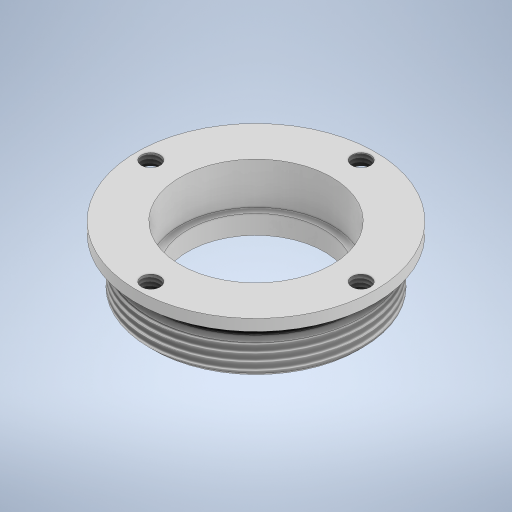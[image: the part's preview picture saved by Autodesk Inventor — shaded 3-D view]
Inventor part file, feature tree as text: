
AUTODESK INVENTOR PART (.ipt)
format: ipt  version: 2023 (Build 270158000, 158)  size: 316,416 bytes
history: native  units: mm
features: sketch x2, revolve x1, chamfer x1, thread x1, hole x1, pattern_circular x1
ambient origin geometry x8: Origin, YZ Plane, XZ Plane, XY Plane, X Axis, Y Axis, Z Axis, Center Point
bodies: Solid1 (feature_tree)
feature tree (7):
  revolve  "Revolution1"  [1 undecoded]
  chamfer  "Chamfer1"  Distance=4.5mm
  thread  "Thread1"  [1 undecoded]
  hole  "Hole2"  [1 undecoded]
  pattern_circular  "Circular Pattern2"  Angle=45.0deg  [1 undecoded]
  sketch  "Sketch1"  dims[d0=18.0mm d2=2.0mm]
  sketch  "Sketch3"  dims[d3=2.0mm d4=4.5mm d5=20.0mm d6=360.0deg d8=0.5mm d9=2.0mm d10=45.0deg d11=3.5mm d12=0.0mm d13=28.0mm d14=1.5mm d15=31.5mm d28=2.0mm d29=2.459mm d30=6.0mm d31=5.0mm d32=10.0mm d33=90.0deg d34=8.8mm d35=0.0mm d36=40.0mm d37=360.0deg]
note: 4 required parameter values undecoded (feature->parameter linkage not recoverable at this tier; creation-order binding heuristic only, values carry confidence <= 0.55)